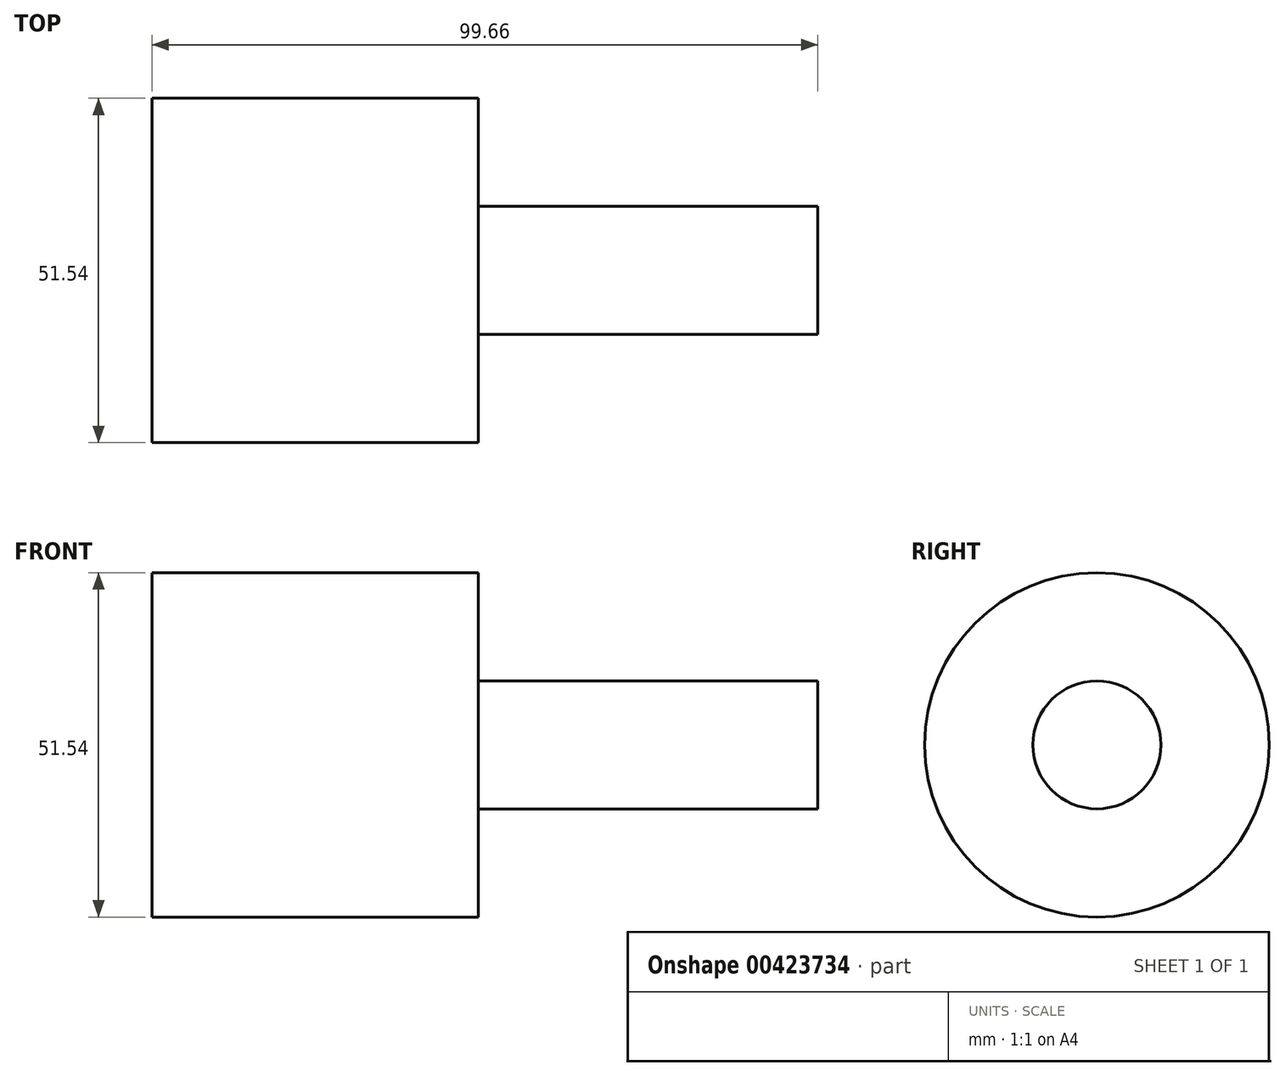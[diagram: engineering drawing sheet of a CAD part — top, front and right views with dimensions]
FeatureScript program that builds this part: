
annotation { "Feature Type Name" : "Feature", "Feature Type Description" : "" }
export const myFeature = defineFeature(function(context is Context, id is Id, definition is map)
    precondition{}
    {
        {
            var Q0;
            Q0=qCreatedBy(makeId("Front.planeOp"),FACE);
            var sketch = newSketch(context, id + "F0", { "sketchPlane" : qUnion([Q0])});
            skLineSegment(sketch, "E0", {"start": v(-175.71, 0) * mm, "end": v(124.61, 0) * mm, "construction": true});
            skLineSegment(sketch, "E1.bottom", {"start": v(0, 0) * mm, "end": v(48.86, 0) * mm});
            skLineSegment(sketch, "E1.top", {"start": v(0, 25.77) * mm, "end": v(48.86, 25.77) * mm});
            skLineSegment(sketch, "E1.left", {"start": v(0, 0) * mm, "end": v(0, 25.77) * mm});
            skLineSegment(sketch, "E1.right", {"start": v(48.86, 0) * mm, "end": v(48.86, 25.77) * mm});
            skSolve(sketch);
        }
        {
            var Q0;
            Q0=makeQuery(id+"F0.imprint","IMPRINT",FACE,{"disambiguationData":[TD([[makeQuery(id+"F0.imprint","IMPRINT",EDGE,{"derivedFrom":sQuery(id+"F0.wireOp",EDGE,"E1.bottom")}),1.0]])]});
            var Q1;
            Q1=sQuery(id+"F0.wireOp",EDGE,"E0");
            revolve(context, id + "F1", {"entities" : qUnion([Q0]), "axis" : qUnion([Q1]), "revolveType" : RevolveType.FULL});
        }
        {
            var Q0;
            Q0=makeQuery(id+"F1.opRevolve","SWEPT_FACE",FACE,{"disambiguationData":[OSD([sQuery(id+"F0.wireOp",EDGE,"E1.right")])]});
            var sketch = newSketch(context, id + "F2", { "sketchPlane" : qUnion([Q0])});
            skCircle(sketch, "E2", {"center": v(0, 0) * mm, "radius": 9.57 * mm});
            skSolve(sketch);
        }
        {
            var Q0;
            Q0=makeQuery(id+"F2.imprint","IMPRINT",FACE,{"disambiguationData":[TD([[makeQuery(id+"F2.imprint","IMPRINT",EDGE,{"derivedFrom":sQuery(id+"F2.wireOp",EDGE,"E2")}),1.0]])]});
            extrude(context, id + "F3", {"entities" : qUnion([Q0]), "operationType" : NewBodyOperationType.ADD, "depth" : 50.8 * mm});
        }
    });
